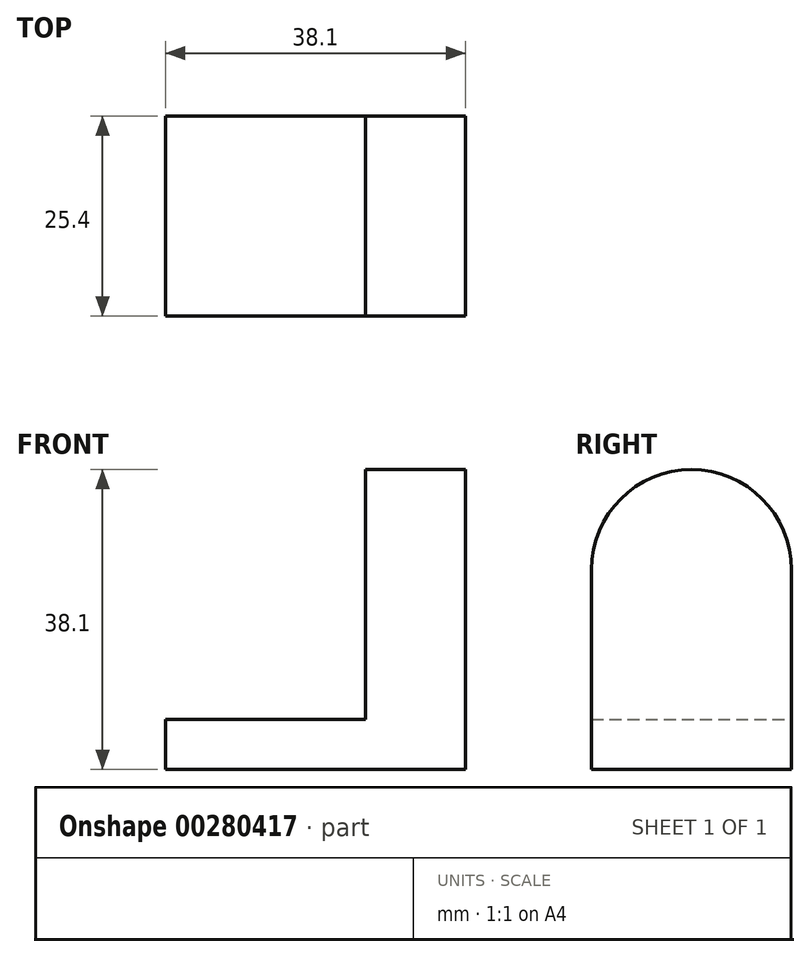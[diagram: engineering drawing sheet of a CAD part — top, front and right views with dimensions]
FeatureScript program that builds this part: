
annotation { "Feature Type Name" : "Feature", "Feature Type Description" : "" }
export const myFeature = defineFeature(function(context is Context, id is Id, definition is map)
    precondition{}
    {
        {
            var Q0;
            Q0=qCreatedBy(makeId("Right.planeOp"),FACE);
            var sketch = newSketch(context, id + "F0", { "sketchPlane" : qUnion([Q0])});
            skLineSegment(sketch, "E0.top", {"start": v(0, 0) * mm, "end": v(25.4, 0) * mm});
            skLineSegment(sketch, "E0.left", {"start": v(0, 25.4) * mm, "end": v(0, 0) * mm});
            skLineSegment(sketch, "E0.right", {"start": v(25.4, 25.4) * mm, "end": v(25.4, 0) * mm});
            skArc(sketch, "E1", {"start": v(25.4, 25.4) * mm, "mid": v(12.7, 38.1) * mm, "end": v(0, 25.4) * mm});
            skSolve(sketch);
        }
        {
            var Q0;
            Q0 = qSketchRegion(id + "F0", true);
            extrude(context, id + "F1", {"entities" : qUnion([Q0]), "depth" : 38.1 * mm});
        }
        {
            var Q0;
            Q0=qCreatedBy(makeId("Right.planeOp"),FACE);
            var sketch = newSketch(context, id + "F2", { "sketchPlane" : qUnion([Q0])});
            skLineSegment(sketch, "E2.bottom", {"start": v(0, 107.95) * mm, "end": v(106.5, 107.95) * mm});
            skLineSegment(sketch, "E2.top", {"start": v(0, 6.35) * mm, "end": v(106.5, 6.35) * mm});
            skLineSegment(sketch, "E2.left", {"start": v(0, 107.95) * mm, "end": v(0, 6.35) * mm});
            skLineSegment(sketch, "E2.right", {"start": v(106.5, 107.95) * mm, "end": v(106.5, 6.35) * mm});
            skSolve(sketch);
        }
        {
            var Q0;
            Q0 = qSketchRegion(id + "F2", true);
            extrude(context, id + "F3", {"entities" : qUnion([Q0]), "operationType" : NewBodyOperationType.REMOVE, "depth" : 25.4 * mm});
        }
    });
